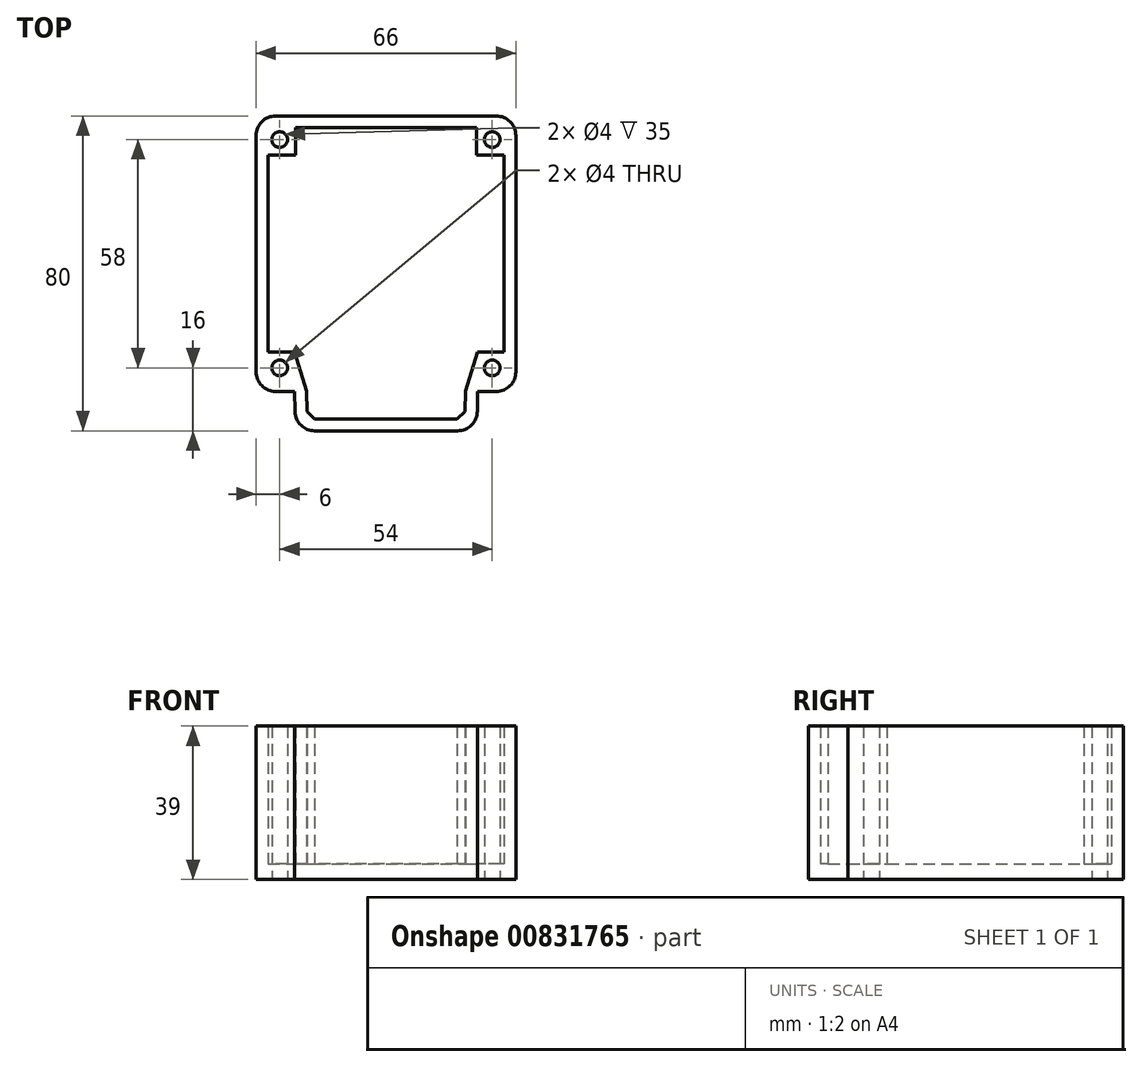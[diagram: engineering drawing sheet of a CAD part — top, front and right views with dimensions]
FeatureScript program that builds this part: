
annotation { "Feature Type Name" : "Feature", "Feature Type Description" : "" }
export const myFeature = defineFeature(function(context is Context, id is Id, definition is map)
    precondition{}
    {
        {
            var Q0;
            Q0=qCreatedBy(makeId("Top.planeOp"),FACE);
            var sketch = newSketch(context, id + "F0", { "sketchPlane" : qUnion([Q0])});
            skLineSegment(sketch, "E0.bottom", {"start": v(4.9, 0) * mm, "end": v(41.2, 0) * mm});
            skLineSegment(sketch, "E0.left", {"start": v(-0.1, 4.9) * mm, "end": v(-0.2, 10) * mm});
            skLineSegment(sketch, "E1", {"start": v(23.1, 5) * mm, "end": v(23.1, 0) * mm, "construction": true});
            skPoint(sketch, "E1.startSnap0", {"position": v(23.1, 0) * mm});
            skPoint(sketch, "E2.endSnap0", {"position": v(3.75, 15) * mm});
            skLineSegment(sketch, "E3.bottom", {"start": v(46.2, 10) * mm, "end": v(51, 10) * mm});
            skLineSegment(sketch, "E3.right", {"start": v(56, 15) * mm, "end": v(56, 15) * mm});
            skCircle(sketch, "E4", {"center": v(50, 16) * mm, "radius": 2 * mm});
            skPoint(sketch, "E4.centerSnap0", {"position": v(50, 21) * mm});
            skLineSegment(sketch, "E5.MirrorCS", {"start": v(-10, 15) * mm, "end": v(-10, 15) * mm});
            skLineSegment(sketch, "E6.MirrorCS", {"start": v(-0.2, 10) * mm, "end": v(-5, 10) * mm});
            skPoint(sketch, "E7.visualSharp", {"position": v(56, 20) * mm});
            skPoint(sketch, "E8.visualSharp", {"position": v(56, 10) * mm});
            skArc(sketch, "E8.filletArc", {"start": v(51, 10) * mm, "mid": v(54.54, 11.46) * mm, "end": v(56, 15) * mm});
            skPoint(sketch, "E9.visualSharp", {"position": v(-10, 20) * mm});
            skPoint(sketch, "E10.visualSharp", {"position": v(-10, 10) * mm});
            skArc(sketch, "E10.filletArc", {"start": v(-10, 15) * mm, "mid": v(-8.54, 11.46) * mm, "end": v(-5, 10) * mm});
            skLineSegment(sketch, "E11", {"start": v(-10, 30) * mm, "end": v(-10, 75) * mm});
            skLineSegment(sketch, "E12", {"start": v(-5, 80) * mm, "end": v(51, 80) * mm});
            skLineSegment(sketch, "E13", {"start": v(56, 75) * mm, "end": v(56, 30) * mm});
            skLineSegment(sketch, "E14", {"start": v(-10, 15) * mm, "end": v(-10, 30) * mm});
            skLineSegment(sketch, "E15", {"start": v(56, 15) * mm, "end": v(56, 30) * mm});
            skLineSegment(sketch, "E16", {"start": v(46.2, 5) * mm, "end": v(46.2, 10) * mm});
            skCircle(sketch, "E17", {"center": v(-4, 74) * mm, "radius": 2 * mm});
            skLineSegment(sketch, "E18", {"start": v(23, -7.31) * mm, "end": v(23, 89.93) * mm, "construction": true});
            skCircle(sketch, "E19.MirrorC", {"center": v(50, 74) * mm, "radius": 2 * mm});
            skCircle(sketch, "E20.MirrorC", {"center": v(-4, 16) * mm, "radius": 2 * mm});
            skPoint(sketch, "E21.visualSharp", {"position": v(0, 0) * mm});
            skArc(sketch, "E21.filletArc", {"start": v(-0.1, 4.9) * mm, "mid": v(1.4, 1.43) * mm, "end": v(4.9, 0) * mm});
            skPoint(sketch, "E22.visualSharp", {"position": v(46.2, 0) * mm});
            skArc(sketch, "E22.filletArc", {"start": v(41.2, 0) * mm, "mid": v(44.74, 1.46) * mm, "end": v(46.2, 5) * mm});
            skPoint(sketch, "E23.visualSharp", {"position": v(56, 80) * mm});
            skArc(sketch, "E23.filletArc", {"start": v(56, 75) * mm, "mid": v(54.54, 78.54) * mm, "end": v(51, 80) * mm});
            skPoint(sketch, "E24.visualSharp", {"position": v(-10, 80) * mm});
            skArc(sketch, "E24.filletArc", {"start": v(-5, 80) * mm, "mid": v(-8.54, 78.54) * mm, "end": v(-10, 75) * mm});
            skLineSegment(sketch, "E25", {"start": v(-7, 70) * mm, "end": v(0, 70) * mm});
            skLineSegment(sketch, "E26", {"start": v(0, 70) * mm, "end": v(0, 77) * mm});
            skLineSegment(sketch, "E27.0", {"start": v(-7, 30) * mm, "end": v(-7, 70) * mm});
            skLineSegment(sketch, "E28.0", {"start": v(-7, 20) * mm, "end": v(-7, 30) * mm});
            skLineSegment(sketch, "E29.0", {"start": v(2.9, 4.96) * mm, "end": v(2.8, 10.06) * mm});
            skLineSegment(sketch, "E30.0", {"start": v(4.9, 3) * mm, "end": v(23.1, 3) * mm});
            skLineSegment(sketch, "E31.0", {"start": v(0, 77) * mm, "end": v(23, 77) * mm});
            skLineSegment(sketch, "E32", {"start": v(2.9, 4.96) * mm, "end": v(4.9, 3) * mm});
            skLineSegment(sketch, "E33", {"start": v(-7, 20) * mm, "end": v(-0.2, 20) * mm});
            skLineSegment(sketch, "E34", {"start": v(2.8, 10.06) * mm, "end": v(-0.2, 20) * mm});
            skLineSegment(sketch, "E35.MirrorCS", {"start": v(46, 77) * mm, "end": v(23, 77) * mm});
            skLineSegment(sketch, "E36.MirrorCS", {"start": v(46, 70) * mm, "end": v(46, 77) * mm});
            skLineSegment(sketch, "E37.MirrorCS", {"start": v(53, 70) * mm, "end": v(46, 70) * mm});
            skLineSegment(sketch, "E38.MirrorCS", {"start": v(53, 30) * mm, "end": v(53, 70) * mm});
            skLineSegment(sketch, "E39.MirrorCS", {"start": v(53, 20) * mm, "end": v(53, 30) * mm});
            skLineSegment(sketch, "E40.MirrorCS", {"start": v(53, 20) * mm, "end": v(46.2, 20) * mm});
            skLineSegment(sketch, "E41.MirrorCS", {"start": v(43.2, 10.06) * mm, "end": v(46.2, 20) * mm});
            skLineSegment(sketch, "E42.MirrorCS", {"start": v(43.1, 4.96) * mm, "end": v(43.2, 10.06) * mm});
            skLineSegment(sketch, "E43.MirrorCS", {"start": v(41.1, 3) * mm, "end": v(22.9, 3) * mm});
            skLineSegment(sketch, "E44.MirrorCS", {"start": v(43.1, 4.96) * mm, "end": v(41.1, 3) * mm});
            skSolve(sketch);
        }
        {
            var Q0;
            Q0=makeQuery(id+"F0.imprint","IMPRINT",FACE,{"disambiguationData":[TD([[makeQuery(id+"F0.imprint","IMPRINT",EDGE,{"derivedFrom":sQuery(id+"F0.wireOp",EDGE,"E0.bottom")}),1.0]])]});
            extrude(context, id + "F1", {"entities" : qUnion([Q0]), "depth" : 35 * mm, "offsetDistance" : 25 * mm});
        }
        {
            var Q0;
            Q0=makeQuery(id+"F0.imprint","IMPRINT",FACE,{"disambiguationData":[TD([[makeQuery(id+"F0.imprint","IMPRINT",EDGE,{"derivedFrom":sQuery(id+"F0.wireOp",EDGE,"E0.bottom")}),1.0]])]});
            var Q1;
            Q1=makeQuery(id+"F0.imprint","IMPRINT",FACE,{"disambiguationData":[TD([[makeQuery(id+"F0.imprint","IMPRINT",EDGE,{"derivedFrom":sQuery(id+"F0.wireOp",EDGE,"E25")}),-1.0]])]});
            var Q2;
            Q2=makeQuery(id+"F0.imprint","IMPRINT",FACE,{"disambiguationData":[TD([[makeQuery(id+"F0.imprint","IMPRINT",EDGE,{"derivedFrom":sQuery(id+"F0.wireOp",EDGE,"E19.MirrorC")}),-1.0]])]});
            var Q3;
            Q3=makeQuery(id+"F0.imprint","IMPRINT",FACE,{"disambiguationData":[TD([[makeQuery(id+"F0.imprint","IMPRINT",EDGE,{"derivedFrom":sQuery(id+"F0.wireOp",EDGE,"E17")}),1.0]])]});
            var Q4;
            Q4=makeQuery(id+"F0.imprint","IMPRINT",FACE,{"disambiguationData":[TD([[makeQuery(id+"F0.imprint","IMPRINT",EDGE,{"derivedFrom":sQuery(id+"F0.wireOp",EDGE,"E20.MirrorC")}),-1.0]])]});
            var Q5;
            Q5=makeQuery(id+"F0.imprint","IMPRINT",FACE,{"disambiguationData":[TD([[makeQuery(id+"F0.imprint","IMPRINT",EDGE,{"derivedFrom":sQuery(id+"F0.wireOp",EDGE,"E4")}),1.0]])]});
            extrude(context, id + "F2", {"entities" : qUnion([Q0, Q1, Q2, Q3, Q4, Q5]), "operationType" : NewBodyOperationType.ADD, "oppositeDirection" : true, "depth" : 4 * mm, "offsetDistance" : 25 * mm});
        }
    });
